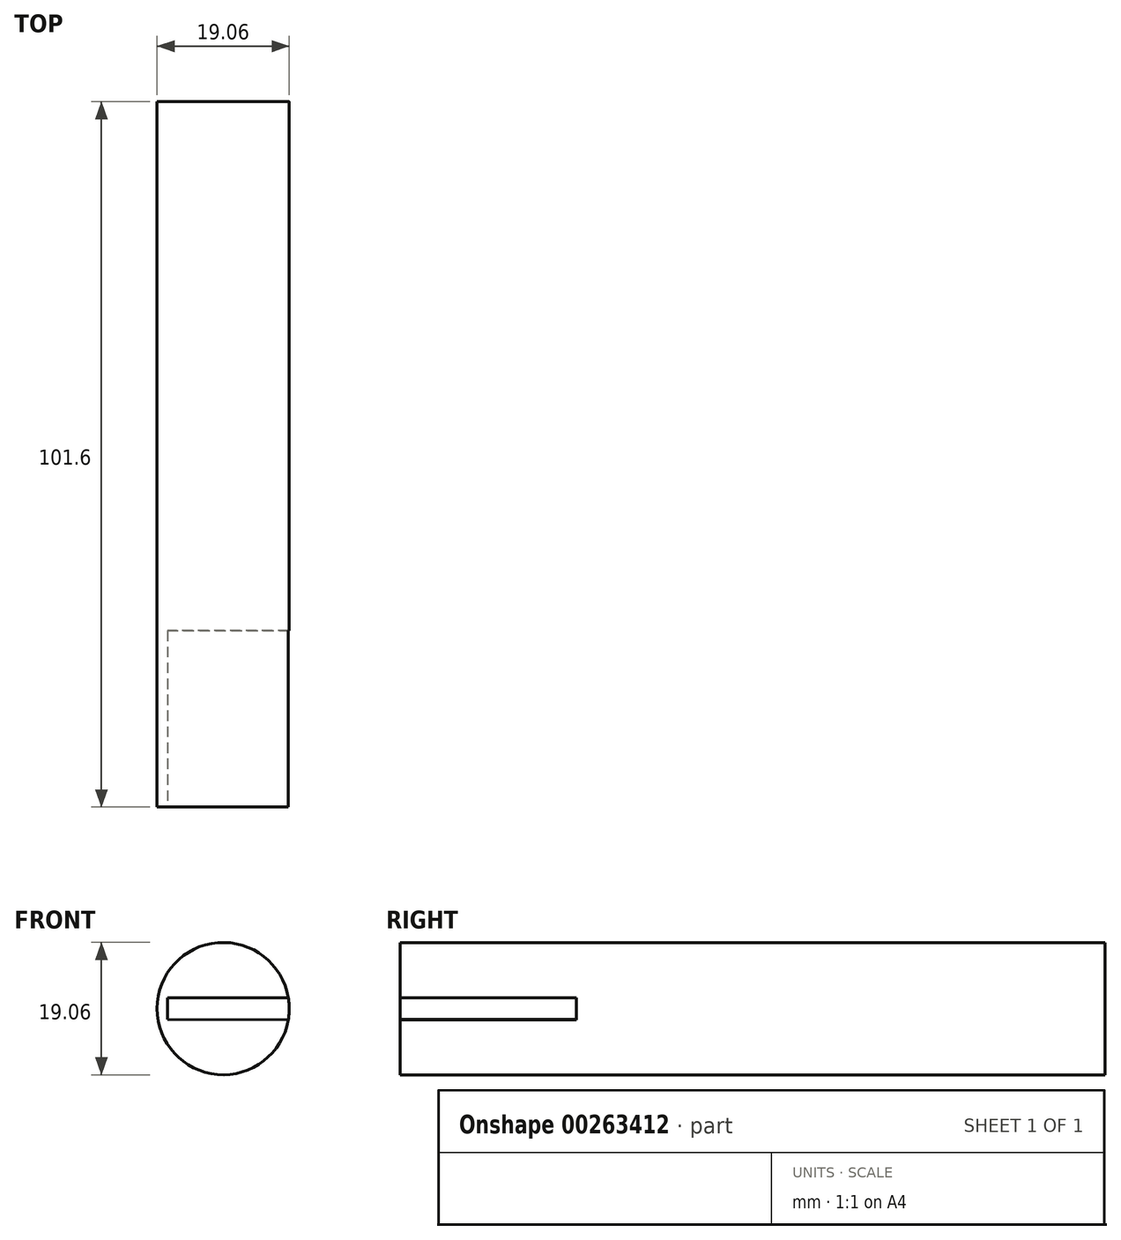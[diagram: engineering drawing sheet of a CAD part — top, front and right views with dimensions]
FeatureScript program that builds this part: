
annotation { "Feature Type Name" : "Feature", "Feature Type Description" : "" }
export const myFeature = defineFeature(function(context is Context, id is Id, definition is map)
    precondition{}
    {
        {
            var Q0;
            Q0=qCreatedBy(makeId("Front.planeOp"),FACE);
            var sketch = newSketch(context, id + "F0", { "sketchPlane" : qUnion([Q0])});
            skCircle(sketch, "E0", {"center": v(0, 0) * mm, "radius": 9.53 * mm});
            skSolve(sketch);
        }
        {
            var Q0;
            Q0 = qSketchRegion(id + "F0", true);
            extrude(context, id + "F1", {"entities" : qUnion([Q0]), "depth" : 101.6 * mm});
        }
        {
            var Q0;
            Q0=makeQuery(id+"F1.opExtrude","CAP_FACE",FACE,{"disambiguationData":[OSD([sQuery(id+"F0.wireOp",EDGE,"E0")])],"isStart":false});
            var sketch = newSketch(context, id + "F2", { "sketchPlane" : qUnion([Q0])});
            skLineSegment(sketch, "E1.right", {"start": v(-8.01, -1.58) * mm, "end": v(-8.01, 1.57) * mm});
            skLineSegment(sketch, "E2", {"start": v(-8.01, 1.57) * mm, "end": v(9.6, 1.57) * mm});
            skLineSegment(sketch, "E3", {"start": v(9.6, 1.57) * mm, "end": v(9.6, -1.6) * mm});
            skLineSegment(sketch, "E4", {"start": v(9.6, -1.6) * mm, "end": v(-8.01, -1.58) * mm});
            skSolve(sketch);
        }
        {
            var Q0;
            Q0 = qSketchRegion(id + "F2", true);
            extrude(context, id + "F3", {"entities" : qUnion([Q0]), "operationType" : NewBodyOperationType.REMOVE, "oppositeDirection" : true, "depth" : 25.4 * mm});
        }
    });
